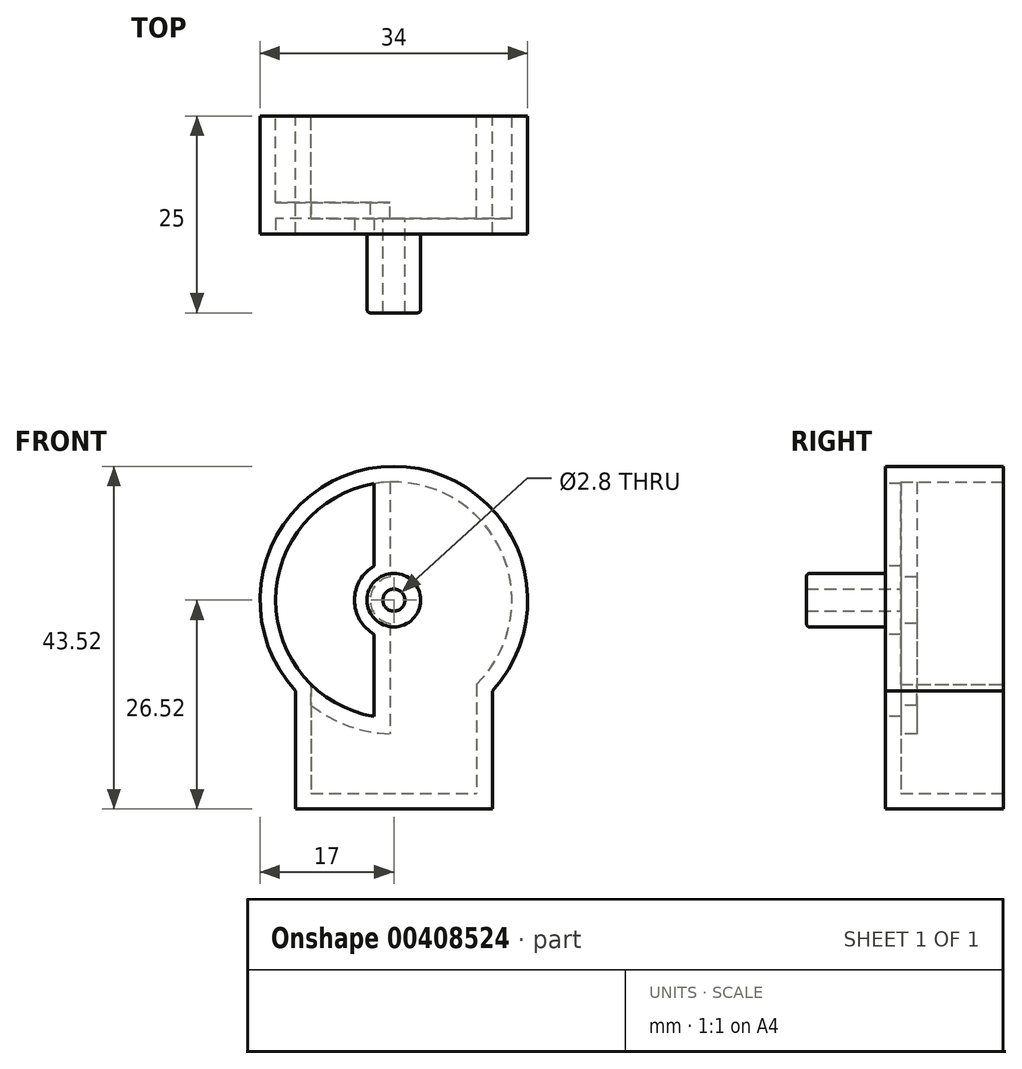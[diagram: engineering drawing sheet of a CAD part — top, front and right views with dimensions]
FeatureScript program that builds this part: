
annotation { "Feature Type Name" : "Feature", "Feature Type Description" : "" }
export const myFeature = defineFeature(function(context is Context, id is Id, definition is map)
    precondition{}
    {
        {
            var Q0;
            Q0=qCreatedBy(makeId("Front.planeOp"),FACE);
            var sketch = newSketch(context, id + "F0", { "sketchPlane" : qUnion([Q0])});
            skCircle(sketch, "E0", {"center": v(0, 0) * mm, "radius": 17 * mm});
            skLineSegment(sketch, "E1.bottom", {"start": v(-12.5, -11.52) * mm, "end": v(12.5, -11.52) * mm, "construction": true});
            skLineSegment(sketch, "E1.top", {"start": v(-12.5, -26.52) * mm, "end": v(12.5, -26.52) * mm});
            skLineSegment(sketch, "E1.left", {"start": v(-12.5, -11.52) * mm, "end": v(-12.5, -26.52) * mm});
            skLineSegment(sketch, "E1.right", {"start": v(12.5, -11.52) * mm, "end": v(12.5, -26.52) * mm});
            skLineSegment(sketch, "E2", {"start": v(0, 0) * mm, "end": v(0, -26.52) * mm, "construction": true});
            skPoint(sketch, "E3", {"position": v(0, -26.52) * mm});
            skSolve(sketch);
        }
        {
            var Q0;
            Q0 = qSketchRegion(id + "F0", true);
            extrude(context, id + "F1", {"entities" : qUnion([Q0]), "depth" : 15 * mm});
        }
        {
            var Q0;
            Q0=makeQuery(id+"F1.opExtrude","CAP_FACE",FACE,{"disambiguationData":[OSD([sQuery(id+"F0.wireOp",EDGE,"E0"),sQuery(id+"F0.wireOp",EDGE,"E1.top"),sQuery(id+"F0.wireOp",EDGE,"E1.left"),sQuery(id+"F0.wireOp",EDGE,"E1.right")])],"isStart":false});
            var sketch = newSketch(context, id + "F2", { "sketchPlane" : qUnion([Q0])});
            skCircle(sketch, "E4", {"center": v(0, 0) * mm, "radius": 15 * mm, "construction": true});
            skCircle(sketch, "E5", {"center": v(0, 0) * mm, "radius": 5 * mm, "construction": true});
            skLineSegment(sketch, "E6", {"start": v(0, 15) * mm, "end": v(0, -15) * mm, "construction": true});
            skArc(sketch, "E7", {"start": v(-2.5, 14.8) * mm, "mid": v(-15, 0) * mm, "end": v(-2.5, -14.8) * mm});
            skArc(sketch, "E8", {"start": v(-2.5, 4.33) * mm, "mid": v(-5, 0) * mm, "end": v(-2.5, -4.33) * mm});
            skLineSegment(sketch, "E9", {"start": v(-2.5, 14.8) * mm, "end": v(-2.5, -14.8) * mm, "construction": true});
            skLineSegment(sketch, "E10", {"start": v(-2.5, -4.33) * mm, "end": v(-2.5, -14.8) * mm});
            skLineSegment(sketch, "E11", {"start": v(-2.5, 14.8) * mm, "end": v(-2.5, 4.33) * mm});
            skSolve(sketch);
        }
        {
            var Q0;
            Q0 = qSketchRegion(id + "F2", true);
            extrude(context, id + "F3", {"entities" : qUnion([Q0]), "operationType" : NewBodyOperationType.REMOVE, "oppositeDirection" : true, "depth" : 2 * mm});
        }
        {
            var Q0;
            Q0=makeQuery(id+"F1.opExtrude","CAP_FACE",FACE,{"disambiguationData":[OSD([sQuery(id+"F0.wireOp",EDGE,"E0"),sQuery(id+"F0.wireOp",EDGE,"E1.top"),sQuery(id+"F0.wireOp",EDGE,"E1.left"),sQuery(id+"F0.wireOp",EDGE,"E1.right")])],"isStart":false});
            var sketch = newSketch(context, id + "F4", { "sketchPlane" : qUnion([Q0])});
            skCircle(sketch, "E12", {"center": v(0, 0) * mm, "radius": 3.4 * mm});
            skSolve(sketch);
        }
        {
            var Q0;
            Q0 = qSketchRegion(id + "F4", true);
            extrude(context, id + "F5", {"entities" : qUnion([Q0]), "operationType" : NewBodyOperationType.ADD, "depth" : 10 * mm});
        }
        {
            var Q0;
            Q0=makeQuery(id+"F1.opExtrude","CAP_FACE",FACE,{"disambiguationData":[OSD([sQuery(id+"F0.wireOp",EDGE,"E0"),sQuery(id+"F0.wireOp",EDGE,"E1.top"),sQuery(id+"F0.wireOp",EDGE,"E1.left"),sQuery(id+"F0.wireOp",EDGE,"E1.right")])],"isStart":true});
            shell(context, id + "F6", {"entities" : qUnion([Q0]), "thickness" : 2 * mm});
        }
        {
            var Q0;
            Q0=makeQuery(id+"F5.opExtrude","CAP_EDGE",EDGE,{"disambiguationData":[OSD([sQuery(id+"F4.wireOp",EDGE,"E12")])],"isStart":true});
            var Q1;
            Q1=makeQuery(id+"F5.opExtrude","CAP_EDGE",EDGE,{"disambiguationData":[OSD([sQuery(id+"F4.wireOp",EDGE,"E12")])],"isStart":false});
            fillet(context, id + "F7", {"entities" : qUnion([Q0, Q1]), "radius" : .4 * mm, "tangentPropagation" : true, "allowEdgeOverflow" : false});
        }
        {
            var Q0;
            {var subQ0=sQuery(id+"F4.wireOp",EDGE,"E12");Q0=makeQuery(id+"F6.opShell","OFFSET_FACE",FACE,{"disambiguationData":[OSD([subQ0]),TDD([makeQuery(id+"F5.opExtrude","CAP_FACE",FACE,{"disambiguationData":[OSD([subQ0])],"isStart":false})])]});}
            extrude(context, id + "F9", {"entities" : qUnion([Q0]), "operationType" : NewBodyOperationType.REMOVE, "oppositeDirection" : true, "depth" : 25 * mm});
        }
    });
